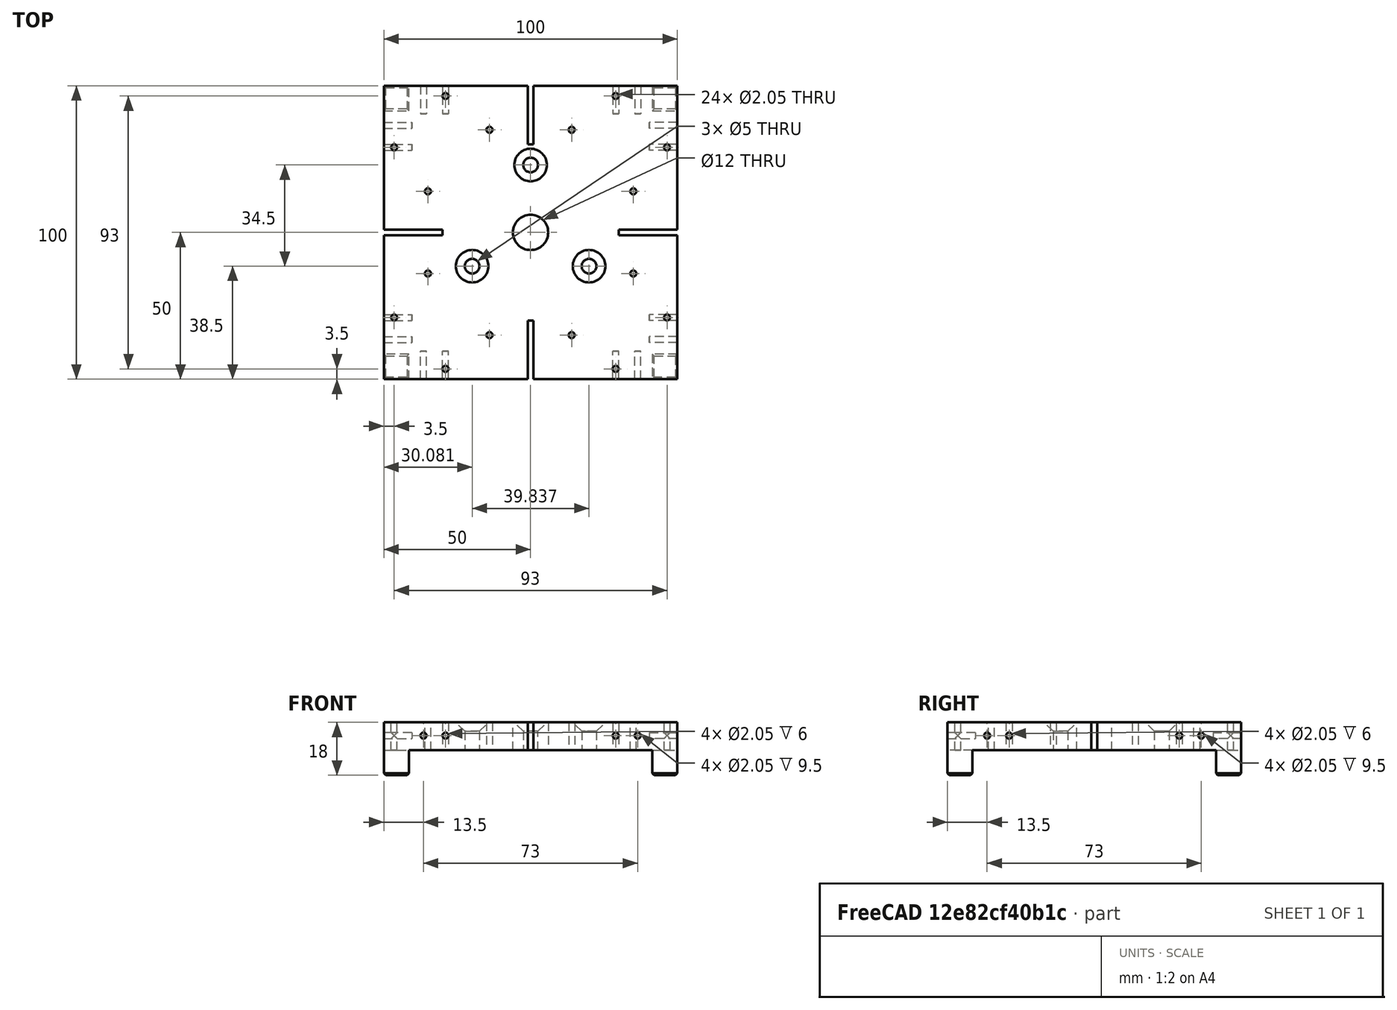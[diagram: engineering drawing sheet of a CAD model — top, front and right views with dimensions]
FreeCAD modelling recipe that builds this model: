
FCSTD DOCUMENT  (FreeCAD 0.20R29603 (Git))
Label: OpenSCAD_MyChassisModeling_NewBottom_version-cnes
License: All rights reserved
LicenseURL: http://en.wikipedia.org/wiki/All_rights_reserved
objects: Part::Fuse×65, Part::Box×61, Part::Cylinder×55, Part::MultiFuse×18, TechDraw::DrawViewDimension×18, Part::Cut×10, TechDraw::DrawViewPart×5, Part::Mirroring×4, TechDraw::DrawViewAnnotation×4, Part::Cone×3, TechDraw::DrawViewSection×2, Part::FeaturePython×1, TechDraw::DrawSVGTemplate×1, TechDraw::DrawPage×1
note: 217 computed .brp shape members not serialized (recipe doc carries the construction recipe); baked Part::Feature solids carry a one-line shape summary decoded from their .brp

FEATURE [Part::Box] cube
  AttacherType = Attacher::AttachEngine3D
  Height = 18
  Length = 8.5
  Placement = pos=(-4.25,-4.25,-18) rot=(0,0,1;0rad)
  Width = 8.5
FEATURE [Part::Box] cube001
  AttacherType = Attacher::AttachEngine3D
  Height = 100
  Length = 9.5
  Placement = pos=(-4.75,42.3466,-38.7141) rot=(1,0,0;0.785398rad)
  Width = 9.5
FEATURE [Part::Box] cube002
  AttacherType = Attacher::AttachEngine3D
  Height = 100
  Length = 9.5
  Placement = pos=(-42.3466,-4.75,-38.7141) rot=(0.357407,0.357407,0.862856;1.71777rad)
  Width = 9.5
FEATURE [Part::Fuse] Group
  Base = -> cube001
  Tool = -> cube002
FEATURE [Part::Box] cube003
  AttacherType = Attacher::AttachEngine3D
  Height = 100
  Length = 9.5
  Placement = pos=(-4.75,42.3466,-38.7141) rot=(1,0,0;0.785398rad)
  Width = 9.5
FEATURE [Part::Box] cube004
  AttacherType = Attacher::AttachEngine3D
  Height = 100
  Length = 9.5
  Placement = pos=(4.75,-42.3466,-38.7141) rot=(0,0.382683,0.92388;3.14159rad)
  Width = 9.5
FEATURE [Part::Fuse] Group001
  Base = -> cube003
  Tool = -> cube004
FEATURE [Part::Box] cube005
  AttacherType = Attacher::AttachEngine3D
  Height = 100
  Length = 9.5
  Placement = pos=(-4.75,42.3466,-38.7141) rot=(1,0,0;0.785398rad)
  Width = 9.5
FEATURE [Part::Box] cube006
  AttacherType = Attacher::AttachEngine3D
  Height = 100
  Length = 9.5
  Placement = pos=(42.3466,4.75,-38.7141) rot=(0.357407,-0.357407,-0.862856;1.71777rad)
  Width = 9.5
FEATURE [Part::Fuse] Group002
  Base = -> cube005
  Tool = -> cube006
FEATURE [Part::MultiFuse] Group003
  Shapes = -> [Group,Group001,Group002]
FEATURE [Part::Cut] difference
  Base = -> cube
  Placement = pos=(-45.75,-45.75,8.5) rot=(0,0,1;0rad)
  Tool = -> Group003
FEATURE [Part::Box] cube007
  AttacherType = Attacher::AttachEngine3D
  Height = 18
  Length = 8.5
  Placement = pos=(-4.25,-4.25,-18) rot=(0,0,1;0rad)
  Width = 8.5
FEATURE [Part::Box] cube008
  AttacherType = Attacher::AttachEngine3D
  Height = 100
  Length = 9.5
  Placement = pos=(-4.75,42.3466,-38.7141) rot=(1,0,0;0.785398rad)
  Width = 9.5
FEATURE [Part::Box] cube009
  AttacherType = Attacher::AttachEngine3D
  Height = 100
  Length = 9.5
  Placement = pos=(-42.3466,-4.75,-38.7141) rot=(0.357407,0.357407,0.862856;1.71777rad)
  Width = 9.5
FEATURE [Part::Fuse] Group004
  Base = -> cube008
  Tool = -> cube009
FEATURE [Part::Box] cube010
  AttacherType = Attacher::AttachEngine3D
  Height = 100
  Length = 9.5
  Placement = pos=(-4.75,42.3466,-38.7141) rot=(1,0,0;0.785398rad)
  Width = 9.5
FEATURE [Part::Box] cube011
  AttacherType = Attacher::AttachEngine3D
  Height = 100
  Length = 9.5
  Placement = pos=(4.75,-42.3466,-38.7141) rot=(0,0.382683,0.92388;3.14159rad)
  Width = 9.5
FEATURE [Part::Fuse] Group005
  Base = -> cube010
  Tool = -> cube011
FEATURE [Part::Box] cube012
  AttacherType = Attacher::AttachEngine3D
  Height = 100
  Length = 9.5
  Placement = pos=(-4.75,42.3466,-38.7141) rot=(1,0,0;0.785398rad)
  Width = 9.5
FEATURE [Part::Box] cube013
  AttacherType = Attacher::AttachEngine3D
  Height = 100
  Length = 9.5
  Placement = pos=(42.3466,4.75,-38.7141) rot=(0.357407,-0.357407,-0.862856;1.71777rad)
  Width = 9.5
FEATURE [Part::Fuse] Group006
  Base = -> cube012
  Tool = -> cube013
FEATURE [Part::MultiFuse] Group007
  Shapes = -> [Group004,Group005,Group006]
FEATURE [Part::Cut] difference001
  Base = -> cube007
  Placement = pos=(-45.75,-45.75,8.5) rot=(0,0,1;0rad)
  Tool = -> Group007
FEATURE [Part::Fuse] Group008
  Base = -> difference
  Tool = -> difference001
FEATURE [Part::Box] cube014
  AttacherType = Attacher::AttachEngine3D
  Height = 18
  Length = 8.5
  Placement = pos=(-4.25,-4.25,-18) rot=(0,0,1;0rad)
  Width = 8.5
FEATURE [Part::Box] cube015
  AttacherType = Attacher::AttachEngine3D
  Height = 100
  Length = 9.5
  Placement = pos=(-4.75,42.3466,-38.7141) rot=(1,0,0;0.785398rad)
  Width = 9.5
FEATURE [Part::Box] cube016
  AttacherType = Attacher::AttachEngine3D
  Height = 100
  Length = 9.5
  Placement = pos=(-42.3466,-4.75,-38.7141) rot=(0.357407,0.357407,0.862856;1.71777rad)
  Width = 9.5
FEATURE [Part::Fuse] Group009
  Base = -> cube015
  Tool = -> cube016
FEATURE [Part::Box] cube017
  AttacherType = Attacher::AttachEngine3D
  Height = 100
  Length = 9.5
  Placement = pos=(-4.75,42.3466,-38.7141) rot=(1,0,0;0.785398rad)
  Width = 9.5
FEATURE [Part::Box] cube018
  AttacherType = Attacher::AttachEngine3D
  Height = 100
  Length = 9.5
  Placement = pos=(4.75,-42.3466,-38.7141) rot=(0,0.382683,0.92388;3.14159rad)
  Width = 9.5
FEATURE [Part::Fuse] Group010
  Base = -> cube017
  Tool = -> cube018
FEATURE [Part::Box] cube019
  AttacherType = Attacher::AttachEngine3D
  Height = 100
  Length = 9.5
  Placement = pos=(-4.75,42.3466,-38.7141) rot=(1,0,0;0.785398rad)
  Width = 9.5
FEATURE [Part::Box] cube020
  AttacherType = Attacher::AttachEngine3D
  Height = 100
  Length = 9.5
  Placement = pos=(42.3466,4.75,-38.7141) rot=(0.357407,-0.357407,-0.862856;1.71777rad)
  Width = 9.5
FEATURE [Part::Fuse] Group011
  Base = -> cube019
  Tool = -> cube020
FEATURE [Part::MultiFuse] Group012
  Shapes = -> [Group009,Group010,Group011]
FEATURE [Part::Cut] difference002
  Base = -> cube014
  Placement = pos=(-45.75,-45.75,8.5) rot=(0,0,1;0rad)
  Tool = -> Group012
FEATURE [Part::Box] cube021
  AttacherType = Attacher::AttachEngine3D
  Height = 18
  Length = 8.5
  Placement = pos=(-4.25,-4.25,-18) rot=(0,0,1;0rad)
  Width = 8.5
FEATURE [Part::Box] cube022
  AttacherType = Attacher::AttachEngine3D
  Height = 100
  Length = 9.5
  Placement = pos=(-4.75,42.3466,-38.7141) rot=(1,0,0;0.785398rad)
  Width = 9.5
FEATURE [Part::Box] cube023
  AttacherType = Attacher::AttachEngine3D
  Height = 100
  Length = 9.5
  Placement = pos=(-42.3466,-4.75,-38.7141) rot=(0.357407,0.357407,0.862856;1.71777rad)
  Width = 9.5
FEATURE [Part::Fuse] Group013
  Base = -> cube022
  Tool = -> cube023
FEATURE [Part::Box] cube024
  AttacherType = Attacher::AttachEngine3D
  Height = 100
  Length = 9.5
  Placement = pos=(-4.75,42.3466,-38.7141) rot=(1,0,0;0.785398rad)
  Width = 9.5
FEATURE [Part::Box] cube025
  AttacherType = Attacher::AttachEngine3D
  Height = 100
  Length = 9.5
  Placement = pos=(4.75,-42.3466,-38.7141) rot=(0,0.382683,0.92388;3.14159rad)
  Width = 9.5
FEATURE [Part::Fuse] Group014
  Base = -> cube024
  Tool = -> cube025
FEATURE [Part::Box] cube026
  AttacherType = Attacher::AttachEngine3D
  Height = 100
  Length = 9.5
  Placement = pos=(-4.75,42.3466,-38.7141) rot=(1,0,0;0.785398rad)
  Width = 9.5
FEATURE [Part::Box] cube027
  AttacherType = Attacher::AttachEngine3D
  Height = 100
  Length = 9.5
  Placement = pos=(42.3466,4.75,-38.7141) rot=(0.357407,-0.357407,-0.862856;1.71777rad)
  Width = 9.5
FEATURE [Part::Fuse] Group015
  Base = -> cube026
  Tool = -> cube027
FEATURE [Part::MultiFuse] Group016
  Shapes = -> [Group013,Group014,Group015]
FEATURE [Part::Cut] difference003
  Base = -> cube021
  Placement = pos=(45.75,-45.75,8.5) rot=(0,0,1;1.5708rad)
  Tool = -> Group016
FEATURE [Part::Fuse] Group017
  Base = -> difference002
  Tool = -> difference003
FEATURE [Part::Box] cube028
  AttacherType = Attacher::AttachEngine3D
  Height = 18
  Length = 8.5
  Placement = pos=(-4.25,-4.25,-18) rot=(0,0,1;0rad)
  Width = 8.5
FEATURE [Part::Box] cube029
  AttacherType = Attacher::AttachEngine3D
  Height = 100
  Length = 9.5
  Placement = pos=(-4.75,42.3466,-38.7141) rot=(1,0,0;0.785398rad)
  Width = 9.5
FEATURE [Part::Box] cube030
  AttacherType = Attacher::AttachEngine3D
  Height = 100
  Length = 9.5
  Placement = pos=(-42.3466,-4.75,-38.7141) rot=(0.357407,0.357407,0.862856;1.71777rad)
  Width = 9.5
FEATURE [Part::Fuse] Group018
  Base = -> cube029
  Tool = -> cube030
FEATURE [Part::Box] cube031
  AttacherType = Attacher::AttachEngine3D
  Height = 100
  Length = 9.5
  Placement = pos=(-4.75,42.3466,-38.7141) rot=(1,0,0;0.785398rad)
  Width = 9.5
FEATURE [Part::Box] cube032
  AttacherType = Attacher::AttachEngine3D
  Height = 100
  Length = 9.5
  Placement = pos=(4.75,-42.3466,-38.7141) rot=(0,0.382683,0.92388;3.14159rad)
  Width = 9.5
FEATURE [Part::Fuse] Group019
  Base = -> cube031
  Tool = -> cube032
FEATURE [Part::Box] cube033
  AttacherType = Attacher::AttachEngine3D
  Height = 100
  Length = 9.5
  Placement = pos=(-4.75,42.3466,-38.7141) rot=(1,0,0;0.785398rad)
  Width = 9.5
FEATURE [Part::Box] cube034
  AttacherType = Attacher::AttachEngine3D
  Height = 100
  Length = 9.5
  Placement = pos=(42.3466,4.75,-38.7141) rot=(0.357407,-0.357407,-0.862856;1.71777rad)
  Width = 9.5
FEATURE [Part::Fuse] Group020
  Base = -> cube033
  Tool = -> cube034
FEATURE [Part::MultiFuse] Group021
  Shapes = -> [Group018,Group019,Group020]
FEATURE [Part::Cut] difference004
  Base = -> cube028
  Placement = pos=(-45.75,-45.75,8.5) rot=(0,0,1;0rad)
  Tool = -> Group021
FEATURE [Part::Box] cube035
  AttacherType = Attacher::AttachEngine3D
  Height = 18
  Length = 8.5
  Placement = pos=(-4.25,-4.25,-18) rot=(0,0,1;0rad)
  Width = 8.5
FEATURE [Part::Box] cube036
  AttacherType = Attacher::AttachEngine3D
  Height = 100
  Length = 9.5
  Placement = pos=(-4.75,42.3466,-38.7141) rot=(1,0,0;0.785398rad)
  Width = 9.5
FEATURE [Part::Box] cube037
  AttacherType = Attacher::AttachEngine3D
  Height = 100
  Length = 9.5
  Placement = pos=(-42.3466,-4.75,-38.7141) rot=(0.357407,0.357407,0.862856;1.71777rad)
  Width = 9.5
FEATURE [Part::Fuse] Group022
  Base = -> cube036
  Tool = -> cube037
FEATURE [Part::Box] cube038
  AttacherType = Attacher::AttachEngine3D
  Height = 100
  Length = 9.5
  Placement = pos=(-4.75,42.3466,-38.7141) rot=(1,0,0;0.785398rad)
  Width = 9.5
FEATURE [Part::Box] cube039
  AttacherType = Attacher::AttachEngine3D
  Height = 100
  Length = 9.5
  Placement = pos=(4.75,-42.3466,-38.7141) rot=(0,0.382683,0.92388;3.14159rad)
  Width = 9.5
FEATURE [Part::Fuse] Group023
  Base = -> cube038
  Tool = -> cube039
FEATURE [Part::Box] cube040
  AttacherType = Attacher::AttachEngine3D
  Height = 100
  Length = 9.5
  Placement = pos=(-4.75,42.3466,-38.7141) rot=(1,0,0;0.785398rad)
  Width = 9.5
FEATURE [Part::Box] cube041
  AttacherType = Attacher::AttachEngine3D
  Height = 100
  Length = 9.5
  Placement = pos=(42.3466,4.75,-38.7141) rot=(0.357407,-0.357407,-0.862856;1.71777rad)
  Width = 9.5
FEATURE [Part::Fuse] Group024
  Base = -> cube040
  Tool = -> cube041
FEATURE [Part::MultiFuse] Group025
  Shapes = -> [Group022,Group023,Group024]
FEATURE [Part::Cut] difference005
  Base = -> cube035
  Placement = pos=(45.75,45.75,8.5) rot=(0,0,1;3.14159rad)
  Tool = -> Group025
FEATURE [Part::Fuse] Group026
  Base = -> difference004
  Tool = -> difference005
FEATURE [Part::Box] cube042
  AttacherType = Attacher::AttachEngine3D
  Height = 18
  Length = 8.5
  Placement = pos=(-4.25,-4.25,-18) rot=(0,0,1;0rad)
  Width = 8.5
FEATURE [Part::Box] cube043
  AttacherType = Attacher::AttachEngine3D
  Height = 100
  Length = 9.5
  Placement = pos=(-4.75,42.3466,-38.7141) rot=(1,0,0;0.785398rad)
  Width = 9.5
FEATURE [Part::Box] cube044
  AttacherType = Attacher::AttachEngine3D
  Height = 100
  Length = 9.5
  Placement = pos=(-42.3466,-4.75,-38.7141) rot=(0.357407,0.357407,0.862856;1.71777rad)
  Width = 9.5
FEATURE [Part::Fuse] Group027
  Base = -> cube043
  Tool = -> cube044
FEATURE [Part::Box] cube045
  AttacherType = Attacher::AttachEngine3D
  Height = 100
  Length = 9.5
  Placement = pos=(-4.75,42.3466,-38.7141) rot=(1,0,0;0.785398rad)
  Width = 9.5
FEATURE [Part::Box] cube046
  AttacherType = Attacher::AttachEngine3D
  Height = 100
  Length = 9.5
  Placement = pos=(4.75,-42.3466,-38.7141) rot=(0,0.382683,0.92388;3.14159rad)
  Width = 9.5
FEATURE [Part::Fuse] Group028
  Base = -> cube045
  Tool = -> cube046
FEATURE [Part::Box] cube047
  AttacherType = Attacher::AttachEngine3D
  Height = 100
  Length = 9.5
  Placement = pos=(-4.75,42.3466,-38.7141) rot=(1,0,0;0.785398rad)
  Width = 9.5
FEATURE [Part::Box] cube048
  AttacherType = Attacher::AttachEngine3D
  Height = 100
  Length = 9.5
  Placement = pos=(42.3466,4.75,-38.7141) rot=(0.357407,-0.357407,-0.862856;1.71777rad)
  Width = 9.5
FEATURE [Part::Fuse] Group029
  Base = -> cube047
  Tool = -> cube048
FEATURE [Part::MultiFuse] Group030
  Shapes = -> [Group027,Group028,Group029]
FEATURE [Part::Cut] difference006
  Base = -> cube042
  Placement = pos=(-45.75,-45.75,8.5) rot=(0,0,1;0rad)
  Tool = -> Group030
FEATURE [Part::Box] cube049
  AttacherType = Attacher::AttachEngine3D
  Height = 18
  Length = 8.5
  Placement = pos=(-4.25,-4.25,-18) rot=(0,0,1;0rad)
  Width = 8.5
FEATURE [Part::Box] cube050
  AttacherType = Attacher::AttachEngine3D
  Height = 100
  Length = 9.5
  Placement = pos=(-4.75,42.3466,-38.7141) rot=(1,0,0;0.785398rad)
  Width = 9.5
FEATURE [Part::Box] cube051
  AttacherType = Attacher::AttachEngine3D
  Height = 100
  Length = 9.5
  Placement = pos=(-42.3466,-4.75,-38.7141) rot=(0.357407,0.357407,0.862856;1.71777rad)
  Width = 9.5
FEATURE [Part::Fuse] Group031
  Base = -> cube050
  Tool = -> cube051
FEATURE [Part::Box] cube052
  AttacherType = Attacher::AttachEngine3D
  Height = 100
  Length = 9.5
  Placement = pos=(-4.75,42.3466,-38.7141) rot=(1,0,0;0.785398rad)
  Width = 9.5
FEATURE [Part::Box] cube053
  AttacherType = Attacher::AttachEngine3D
  Height = 100
  Length = 9.5
  Placement = pos=(4.75,-42.3466,-38.7141) rot=(0,0.382683,0.92388;3.14159rad)
  Width = 9.5
FEATURE [Part::Fuse] Group032
  Base = -> cube052
  Tool = -> cube053
FEATURE [Part::Box] cube054
  AttacherType = Attacher::AttachEngine3D
  Height = 100
  Length = 9.5
  Placement = pos=(-4.75,42.3466,-38.7141) rot=(1,0,0;0.785398rad)
  Width = 9.5
FEATURE [Part::Box] cube055
  AttacherType = Attacher::AttachEngine3D
  Height = 100
  Length = 9.5
  Placement = pos=(42.3466,4.75,-38.7141) rot=(0.357407,-0.357407,-0.862856;1.71777rad)
  Width = 9.5
FEATURE [Part::Fuse] Group033
  Base = -> cube054
  Tool = -> cube055
FEATURE [Part::MultiFuse] Group034
  Shapes = -> [Group031,Group032,Group033]
FEATURE [Part::Cut] difference007
  Base = -> cube049
  Placement = pos=(-45.75,45.75,8.5) rot=(0,0,-1;1.5708rad)
  Tool = -> Group034
FEATURE [Part::Fuse] Group035
  Base = -> difference006
  Tool = -> difference007
FEATURE [Part::MultiFuse] Group036
  Shapes = -> [Group008,Group017,Group026,Group035]
FEATURE [Part::Box] cube056
  AttacherType = Attacher::AttachEngine3D
  Height = 9.5
  Length = 100
  Placement = pos=(-50,-50,-9.5) rot=(0,0,1;0rad)
  Width = 100
FEATURE [Part::Cylinder] cylinder
  Angle = 360
  AttacherType = Attacher::AttachEngine3D
  FirstAngle = 0
  Height = 11
  Placement = pos=(40.5,-36.5,-5) rot=(0,1,0;1.5708rad)
  Radius = 1.025
  SecondAngle = 0
FEATURE [Part::Cylinder] cylinder001
  Angle = 360
  AttacherType = Attacher::AttachEngine3D
  FirstAngle = 0
  Height = 11
  Placement = pos=(40.5,-29,-5) rot=(0,1,0;1.5708rad)
  Radius = 1.025
  SecondAngle = 0
FEATURE [Part::Fuse] Group037
  Base = -> cylinder
  Tool = -> cylinder001
FEATURE [Part::Cylinder] cylinder002
  Angle = 360
  AttacherType = Attacher::AttachEngine3D
  FirstAngle = 0
  Height = 11
  Placement = pos=(40.5,-36.5,-5) rot=(0,1,0;1.5708rad)
  Radius = 1.025
  SecondAngle = 0
FEATURE [Part::Cylinder] cylinder003
  Angle = 360
  AttacherType = Attacher::AttachEngine3D
  FirstAngle = 0
  Height = 11
  Placement = pos=(40.5,-29,-5) rot=(0,1,0;1.5708rad)
  Radius = 1.025
  SecondAngle = 0
FEATURE [Part::Fuse] Group038
  Base = -> cylinder002
  Tool = -> cylinder003
FEATURE [Part::Mirroring] mirr_Group038  label="mirrored Group038"
  Base = (0,0,0)
  Normal = (0,1,0)
  Source = -> Group038
FEATURE [Part::Fuse] Group039
  Base = -> Group037
  Tool = -> mirr_Group038
FEATURE [Part::Cylinder] cylinder004
  Angle = 360
  AttacherType = Attacher::AttachEngine3D
  FirstAngle = 0
  Height = 11
  Placement = pos=(40.5,-36.5,-5) rot=(0,1,0;1.5708rad)
  Radius = 1.025
  SecondAngle = 0
FEATURE [Part::Cylinder] cylinder005
  Angle = 360
  AttacherType = Attacher::AttachEngine3D
  FirstAngle = 0
  Height = 11
  Placement = pos=(40.5,-29,-5) rot=(0,1,0;1.5708rad)
  Radius = 1.025
  SecondAngle = 0
FEATURE [Part::Fuse] Group040
  Base = -> cylinder004
  Tool = -> cylinder005
FEATURE [Part::Cylinder] cylinder006
  Angle = 360
  AttacherType = Attacher::AttachEngine3D
  FirstAngle = 0
  Height = 11
  Placement = pos=(40.5,-36.5,-5) rot=(0,1,0;1.5708rad)
  Radius = 1.025
  SecondAngle = 0
FEATURE [Part::Cylinder] cylinder007
  Angle = 360
  AttacherType = Attacher::AttachEngine3D
  FirstAngle = 0
  Height = 11
  Placement = pos=(40.5,-29,-5) rot=(0,1,0;1.5708rad)
  Radius = 1.025
  SecondAngle = 0
FEATURE [Part::Fuse] Group041
  Base = -> cylinder006
  Tool = -> cylinder007
FEATURE [Part::Mirroring] mirr_Group041  label="mirrored Group041"
  Base = (0,0,0)
  Normal = (0,1,0)
  Source = -> Group041
FEATURE [Part::Fuse] Group042
  Base = -> Group040
  Placement = pos=(0,0,0) rot=(0,0,1;1.5708rad)
  Tool = -> mirr_Group041
FEATURE [Part::Cylinder] cylinder008
  Angle = 360
  AttacherType = Attacher::AttachEngine3D
  FirstAngle = 0
  Height = 11
  Placement = pos=(40.5,-36.5,-5) rot=(0,1,0;1.5708rad)
  Radius = 1.025
  SecondAngle = 0
FEATURE [Part::Cylinder] cylinder009
  Angle = 360
  AttacherType = Attacher::AttachEngine3D
  FirstAngle = 0
  Height = 11
  Placement = pos=(40.5,-29,-5) rot=(0,1,0;1.5708rad)
  Radius = 1.025
  SecondAngle = 0
FEATURE [Part::Fuse] Group043
  Base = -> cylinder008
  Tool = -> cylinder009
FEATURE [Part::Cylinder] cylinder010
  Angle = 360
  AttacherType = Attacher::AttachEngine3D
  FirstAngle = 0
  Height = 11
  Placement = pos=(40.5,-36.5,-5) rot=(0,1,0;1.5708rad)
  Radius = 1.025
  SecondAngle = 0
FEATURE [Part::Cylinder] cylinder011
  Angle = 360
  AttacherType = Attacher::AttachEngine3D
  FirstAngle = 0
  Height = 11
  Placement = pos=(40.5,-29,-5) rot=(0,1,0;1.5708rad)
  Radius = 1.025
  SecondAngle = 0
FEATURE [Part::Fuse] Group044
  Base = -> cylinder010
  Tool = -> cylinder011
FEATURE [Part::Mirroring] mirr_Group044  label="mirrored Group044"
  Base = (0,0,0)
  Normal = (0,1,0)
  Source = -> Group044
FEATURE [Part::Fuse] Group045
  Base = -> Group043
  Placement = pos=(0,0,0) rot=(0,0,1;3.14159rad)
  Tool = -> mirr_Group044
FEATURE [Part::Cylinder] cylinder012
  Angle = 360
  AttacherType = Attacher::AttachEngine3D
  FirstAngle = 0
  Height = 11
  Placement = pos=(40.5,-36.5,-5) rot=(0,1,0;1.5708rad)
  Radius = 1.025
  SecondAngle = 0
FEATURE [Part::Cylinder] cylinder013
  Angle = 360
  AttacherType = Attacher::AttachEngine3D
  FirstAngle = 0
  Height = 11
  Placement = pos=(40.5,-29,-5) rot=(0,1,0;1.5708rad)
  Radius = 1.025
  SecondAngle = 0
FEATURE [Part::Fuse] Group046
  Base = -> cylinder012
  Tool = -> cylinder013
FEATURE [Part::Cylinder] cylinder014
  Angle = 360
  AttacherType = Attacher::AttachEngine3D
  FirstAngle = 0
  Height = 11
  Placement = pos=(40.5,-36.5,-5) rot=(0,1,0;1.5708rad)
  Radius = 1.025
  SecondAngle = 0
FEATURE [Part::Cylinder] cylinder015
  Angle = 360
  AttacherType = Attacher::AttachEngine3D
  FirstAngle = 0
  Height = 11
  Placement = pos=(40.5,-29,-5) rot=(0,1,0;1.5708rad)
  Radius = 1.025
  SecondAngle = 0
FEATURE [Part::Fuse] Group047
  Base = -> cylinder014
  Tool = -> cylinder015
FEATURE [Part::Mirroring] mirr_Group047  label="mirrored Group047"
  Base = (0,0,0)
  Normal = (0,1,0)
  Source = -> Group047
FEATURE [Part::Fuse] Group048
  Base = -> Group046
  Placement = pos=(0,0,0) rot=(0,0,-1;1.5708rad)
  Tool = -> mirr_Group047
FEATURE [Part::MultiFuse] Group049
  Shapes = -> [Group039,Group042,Group045,Group048]
FEATURE [Part::Cylinder] cylinder016
  Angle = 360
  AttacherType = Attacher::AttachEngine3D
  FirstAngle = 0
  Height = 100
  Placement = pos=(-29,0,-50) rot=(0,0,1;0rad)
  Radius = 1.025
  SecondAngle = 0
FEATURE [Part::Cylinder] cylinder017
  Angle = 360
  AttacherType = Attacher::AttachEngine3D
  FirstAngle = 0
  Height = 100
  Placement = pos=(29,0,-50) rot=(0,0,1;0rad)
  Radius = 1.025
  SecondAngle = 0
FEATURE [Part::Fuse] Matrix_Union
  Base = -> cylinder016
  Placement = pos=(0,46.5,0) rot=(0,0,1;0rad)
  Tool = -> cylinder017
FEATURE [Part::Cylinder] cylinder018
  Angle = 360
  AttacherType = Attacher::AttachEngine3D
  FirstAngle = 0
  Height = 100
  Placement = pos=(-29,0,-50) rot=(0,0,1;0rad)
  Radius = 1.025
  SecondAngle = 0
FEATURE [Part::Cylinder] cylinder019
  Angle = 360
  AttacherType = Attacher::AttachEngine3D
  FirstAngle = 0
  Height = 100
  Placement = pos=(29,0,-50) rot=(0,0,1;0rad)
  Radius = 1.025
  SecondAngle = 0
FEATURE [Part::Fuse] Matrix_Union001
  Base = -> cylinder018
  Placement = pos=(0,46.5,0) rot=(0,0,1;0rad)
  Tool = -> cylinder019
FEATURE [Part::Fuse] Group050
  Base = -> Matrix_Union
  Tool = -> Matrix_Union001
FEATURE [Part::Cylinder] cylinder020
  Angle = 360
  AttacherType = Attacher::AttachEngine3D
  FirstAngle = 0
  Height = 100
  Placement = pos=(-29,0,-50) rot=(0,0,1;0rad)
  Radius = 1.025
  SecondAngle = 0
FEATURE [Part::Cylinder] cylinder021
  Angle = 360
  AttacherType = Attacher::AttachEngine3D
  FirstAngle = 0
  Height = 100
  Placement = pos=(29,0,-50) rot=(0,0,1;0rad)
  Radius = 1.025
  SecondAngle = 0
FEATURE [Part::Fuse] Matrix_Union002
  Base = -> cylinder020
  Placement = pos=(0,46.5,0) rot=(0,0,1;0rad)
  Tool = -> cylinder021
FEATURE [Part::Cylinder] cylinder022
  Angle = 360
  AttacherType = Attacher::AttachEngine3D
  FirstAngle = 0
  Height = 100
  Placement = pos=(-29,0,-50) rot=(0,0,1;0rad)
  Radius = 1.025
  SecondAngle = 0
FEATURE [Part::Cylinder] cylinder023
  Angle = 360
  AttacherType = Attacher::AttachEngine3D
  FirstAngle = 0
  Height = 100
  Placement = pos=(29,0,-50) rot=(0,0,1;0rad)
  Radius = 1.025
  SecondAngle = 0
FEATURE [Part::Fuse] Matrix_Union003
  Base = -> cylinder022
  Placement = pos=(-46.5,0,0) rot=(0,0,1;1.5708rad)
  Tool = -> cylinder023
FEATURE [Part::Fuse] Group051
  Base = -> Matrix_Union002
  Tool = -> Matrix_Union003
FEATURE [Part::Cylinder] cylinder024
  Angle = 360
  AttacherType = Attacher::AttachEngine3D
  FirstAngle = 0
  Height = 100
  Placement = pos=(-29,0,-50) rot=(0,0,1;0rad)
  Radius = 1.025
  SecondAngle = 0
FEATURE [Part::Cylinder] cylinder025
  Angle = 360
  AttacherType = Attacher::AttachEngine3D
  FirstAngle = 0
  Height = 100
  Placement = pos=(29,0,-50) rot=(0,0,1;0rad)
  Radius = 1.025
  SecondAngle = 0
FEATURE [Part::Fuse] Matrix_Union004
  Base = -> cylinder024
  Placement = pos=(0,46.5,0) rot=(0,0,1;0rad)
  Tool = -> cylinder025
FEATURE [Part::Cylinder] cylinder026
  Angle = 360
  AttacherType = Attacher::AttachEngine3D
  FirstAngle = 0
  Height = 100
  Placement = pos=(-29,0,-50) rot=(0,0,1;0rad)
  Radius = 1.025
  SecondAngle = 0
FEATURE [Part::Cylinder] cylinder027
  Angle = 360
  AttacherType = Attacher::AttachEngine3D
  FirstAngle = 0
  Height = 100
  Placement = pos=(29,0,-50) rot=(0,0,1;0rad)
  Radius = 1.025
  SecondAngle = 0
FEATURE [Part::Fuse] Matrix_Union005
  Base = -> cylinder026
  Placement = pos=(-6e-15,-46.5,0) rot=(0,0,1;3.14159rad)
  Tool = -> cylinder027
FEATURE [Part::Fuse] Group052
  Base = -> Matrix_Union004
  Tool = -> Matrix_Union005
FEATURE [Part::Cylinder] cylinder028
  Angle = 360
  AttacherType = Attacher::AttachEngine3D
  FirstAngle = 0
  Height = 100
  Placement = pos=(-29,0,-50) rot=(0,0,1;0rad)
  Radius = 1.025
  SecondAngle = 0
FEATURE [Part::Cylinder] cylinder029
  Angle = 360
  AttacherType = Attacher::AttachEngine3D
  FirstAngle = 0
  Height = 100
  Placement = pos=(29,0,-50) rot=(0,0,1;0rad)
  Radius = 1.025
  SecondAngle = 0
FEATURE [Part::Fuse] Matrix_Union006
  Base = -> cylinder028
  Placement = pos=(0,46.5,0) rot=(0,0,1;0rad)
  Tool = -> cylinder029
FEATURE [Part::Cylinder] cylinder030
  Angle = 360
  AttacherType = Attacher::AttachEngine3D
  FirstAngle = 0
  Height = 100
  Placement = pos=(-29,0,-50) rot=(0,0,1;0rad)
  Radius = 1.025
  SecondAngle = 0
FEATURE [Part::Cylinder] cylinder031
  Angle = 360
  AttacherType = Attacher::AttachEngine3D
  FirstAngle = 0
  Height = 100
  Placement = pos=(29,0,-50) rot=(0,0,1;0rad)
  Radius = 1.025
  SecondAngle = 0
FEATURE [Part::Fuse] Matrix_Union007
  Base = -> cylinder030
  Placement = pos=(46.5,0,0) rot=(0,0,-1;1.5708rad)
  Tool = -> cylinder031
FEATURE [Part::Fuse] Group053
  Base = -> Matrix_Union006
  Tool = -> Matrix_Union007
FEATURE [Part::MultiFuse] Group054
  Shapes = -> [Group050,Group051,Group052,Group053]
FEATURE [Part::Cylinder] cylinder032
  Angle = 360
  AttacherType = Attacher::AttachEngine3D
  FirstAngle = 0
  Height = 100
  Placement = pos=(-14,0,-50) rot=(0,0,1;0rad)
  Radius = 1.025
  SecondAngle = 0
FEATURE [Part::Cylinder] cylinder033
  Angle = 360
  AttacherType = Attacher::AttachEngine3D
  FirstAngle = 0
  Height = 100
  Placement = pos=(14,0,-50) rot=(0,0,1;0rad)
  Radius = 1.025
  SecondAngle = 0
FEATURE [Part::Fuse] Matrix_Union008
  Base = -> cylinder032
  Placement = pos=(0,35,0) rot=(0,0,1;0rad)
  Tool = -> cylinder033
FEATURE [Part::Cylinder] cylinder034
  Angle = 360
  AttacherType = Attacher::AttachEngine3D
  FirstAngle = 0
  Height = 100
  Placement = pos=(-14,0,-50) rot=(0,0,1;0rad)
  Radius = 1.025
  SecondAngle = 0
FEATURE [Part::Cylinder] cylinder035
  Angle = 360
  AttacherType = Attacher::AttachEngine3D
  FirstAngle = 0
  Height = 100
  Placement = pos=(14,0,-50) rot=(0,0,1;0rad)
  Radius = 1.025
  SecondAngle = 0
FEATURE [Part::Fuse] Matrix_Union009
  Base = -> cylinder034
  Placement = pos=(0,35,0) rot=(0,0,1;0rad)
  Tool = -> cylinder035
FEATURE [Part::Fuse] Group055
  Base = -> Matrix_Union008
  Tool = -> Matrix_Union009
FEATURE [Part::Cylinder] cylinder036
  Angle = 360
  AttacherType = Attacher::AttachEngine3D
  FirstAngle = 0
  Height = 100
  Placement = pos=(-14,0,-50) rot=(0,0,1;0rad)
  Radius = 1.025
  SecondAngle = 0
FEATURE [Part::Cylinder] cylinder037
  Angle = 360
  AttacherType = Attacher::AttachEngine3D
  FirstAngle = 0
  Height = 100
  Placement = pos=(14,0,-50) rot=(0,0,1;0rad)
  Radius = 1.025
  SecondAngle = 0
FEATURE [Part::Fuse] Matrix_Union010
  Base = -> cylinder036
  Placement = pos=(0,35,0) rot=(0,0,1;0rad)
  Tool = -> cylinder037
FEATURE [Part::Cylinder] cylinder038
  Angle = 360
  AttacherType = Attacher::AttachEngine3D
  FirstAngle = 0
  Height = 100
  Placement = pos=(-14,0,-50) rot=(0,0,1;0rad)
  Radius = 1.025
  SecondAngle = 0
FEATURE [Part::Cylinder] cylinder039
  Angle = 360
  AttacherType = Attacher::AttachEngine3D
  FirstAngle = 0
  Height = 100
  Placement = pos=(14,0,-50) rot=(0,0,1;0rad)
  Radius = 1.025
  SecondAngle = 0
FEATURE [Part::Fuse] Matrix_Union011
  Base = -> cylinder038
  Placement = pos=(-35,0,0) rot=(0,0,1;1.5708rad)
  Tool = -> cylinder039
FEATURE [Part::Fuse] Group056
  Base = -> Matrix_Union010
  Tool = -> Matrix_Union011
FEATURE [Part::Cylinder] cylinder040
  Angle = 360
  AttacherType = Attacher::AttachEngine3D
  FirstAngle = 0
  Height = 100
  Placement = pos=(-14,0,-50) rot=(0,0,1;0rad)
  Radius = 1.025
  SecondAngle = 0
FEATURE [Part::Cylinder] cylinder041
  Angle = 360
  AttacherType = Attacher::AttachEngine3D
  FirstAngle = 0
  Height = 100
  Placement = pos=(14,0,-50) rot=(0,0,1;0rad)
  Radius = 1.025
  SecondAngle = 0
FEATURE [Part::Fuse] Matrix_Union012
  Base = -> cylinder040
  Placement = pos=(0,35,0) rot=(0,0,1;0rad)
  Tool = -> cylinder041
FEATURE [Part::Cylinder] cylinder042
  Angle = 360
  AttacherType = Attacher::AttachEngine3D
  FirstAngle = 0
  Height = 100
  Placement = pos=(-14,0,-50) rot=(0,0,1;0rad)
  Radius = 1.025
  SecondAngle = 0
FEATURE [Part::Cylinder] cylinder043
  Angle = 360
  AttacherType = Attacher::AttachEngine3D
  FirstAngle = 0
  Height = 100
  Placement = pos=(14,0,-50) rot=(0,0,1;0rad)
  Radius = 1.025
  SecondAngle = 0
FEATURE [Part::Fuse] Matrix_Union013
  Base = -> cylinder042
  Placement = pos=(-4e-15,-35,0) rot=(0,0,1;3.14159rad)
  Tool = -> cylinder043
FEATURE [Part::Fuse] Group057
  Base = -> Matrix_Union012
  Tool = -> Matrix_Union013
FEATURE [Part::Cylinder] cylinder044
  Angle = 360
  AttacherType = Attacher::AttachEngine3D
  FirstAngle = 0
  Height = 100
  Placement = pos=(-14,0,-50) rot=(0,0,1;0rad)
  Radius = 1.025
  SecondAngle = 0
FEATURE [Part::Cylinder] cylinder045
  Angle = 360
  AttacherType = Attacher::AttachEngine3D
  FirstAngle = 0
  Height = 100
  Placement = pos=(14,0,-50) rot=(0,0,1;0rad)
  Radius = 1.025
  SecondAngle = 0
FEATURE [Part::Fuse] Matrix_Union014
  Base = -> cylinder044
  Placement = pos=(0,35,0) rot=(0,0,1;0rad)
  Tool = -> cylinder045
FEATURE [Part::Cylinder] cylinder046
  Angle = 360
  AttacherType = Attacher::AttachEngine3D
  FirstAngle = 0
  Height = 100
  Placement = pos=(-14,0,-50) rot=(0,0,1;0rad)
  Radius = 1.025
  SecondAngle = 0
FEATURE [Part::Cylinder] cylinder047
  Angle = 360
  AttacherType = Attacher::AttachEngine3D
  FirstAngle = 0
  Height = 100
  Placement = pos=(14,0,-50) rot=(0,0,1;0rad)
  Radius = 1.025
  SecondAngle = 0
FEATURE [Part::Fuse] Matrix_Union015
  Base = -> cylinder046
  Placement = pos=(35,0,0) rot=(0,0,-1;1.5708rad)
  Tool = -> cylinder047
FEATURE [Part::Fuse] Group058
  Base = -> Matrix_Union014
  Tool = -> Matrix_Union015
FEATURE [Part::MultiFuse] Group059
  Shapes = -> [Group055,Group056,Group057,Group058]
FEATURE [Part::MultiFuse] union
  Shapes = -> [Group049,Group054,Group059]
FEATURE [Part::Cut] difference008
  Base = -> cube056
  Tool = -> union
FEATURE [Part::Fuse] union001
  Base = -> Group036
  Tool = -> difference008
FEATURE [Part::Cone] cylinder048
  Angle = 360
  AttacherType = Attacher::AttachEngine3D
  Height = 5.55
  Placement = pos=(0,0,-5.55) rot=(0,0,1;0rad)
  Radius1 = 0
  Radius2 = 5.55
FEATURE [Part::Cylinder] cylinder049
  Angle = 360
  AttacherType = Attacher::AttachEngine3D
  FirstAngle = 0
  Height = 0.5
  Radius = 5.55
  SecondAngle = 0
FEATURE [Part::Cylinder] cylinder050
  Angle = 360
  AttacherType = Attacher::AttachEngine3D
  FirstAngle = 0
  Height = 45
  Placement = pos=(0,0,-45) rot=(0,0,1;0rad)
  Radius = 2.5
  SecondAngle = 0
FEATURE [Part::MultiFuse] union002
  Placement = pos=(0,-23,-9.5) rot=(1,0,0;3.14159rad)
  Shapes = -> [cylinder048,cylinder049,cylinder050]
FEATURE [Part::Cone] cylinder051
  Angle = 360
  AttacherType = Attacher::AttachEngine3D
  Height = 5.55
  Placement = pos=(0,0,-5.55) rot=(0,0,1;0rad)
  Radius1 = 0
  Radius2 = 5.55
FEATURE [Part::Cylinder] cylinder052
  Angle = 360
  AttacherType = Attacher::AttachEngine3D
  FirstAngle = 0
  Height = 0.5
  Radius = 5.55
  SecondAngle = 0
FEATURE [Part::Cylinder] cylinder053
  Angle = 360
  AttacherType = Attacher::AttachEngine3D
  FirstAngle = 0
  Height = 45
  Placement = pos=(0,0,-45) rot=(0,0,1;0rad)
  Radius = 2.5
  SecondAngle = 0
FEATURE [Part::MultiFuse] union003
  Placement = pos=(19.9186,11.5,-9.5) rot=(0.5,0.866025,0;3.14159rad)
  Shapes = -> [cylinder051,cylinder052,cylinder053]
FEATURE [Part::Cone] cylinder054
  Angle = 360
  AttacherType = Attacher::AttachEngine3D
  Height = 5.55
  Placement = pos=(0,0,-5.55) rot=(0,0,1;0rad)
  Radius1 = 0
  Radius2 = 5.55
FEATURE [Part::Cylinder] cylinder055
  Angle = 360
  AttacherType = Attacher::AttachEngine3D
  FirstAngle = 0
  Height = 0.5
  Radius = 5.55
  SecondAngle = 0
FEATURE [Part::Cylinder] cylinder056
  Angle = 360
  AttacherType = Attacher::AttachEngine3D
  FirstAngle = 0
  Height = 45
  Placement = pos=(0,0,-45) rot=(0,0,1;0rad)
  Radius = 2.5
  SecondAngle = 0
FEATURE [Part::MultiFuse] union004
  Placement = pos=(-19.9186,11.5,-9.5) rot=(-0.5,0.866025,0;3.14159rad)
  Shapes = -> [cylinder054,cylinder055,cylinder056]
FEATURE [Part::Box] cube057
  AttacherType = Attacher::AttachEngine3D
  Height = 100
  Length = 100
  Placement = pos=(30,-1,-50) rot=(0,0,1;0rad)
  Width = 2
FEATURE [Part::Box] cube058
  AttacherType = Attacher::AttachEngine3D
  Height = 100
  Length = 100
  Placement = pos=(1,30,-50) rot=(0,0,1;1.5708rad)
  Width = 2
FEATURE [Part::Box] cube059
  AttacherType = Attacher::AttachEngine3D
  Height = 100
  Length = 100
  Placement = pos=(-30,1,-50) rot=(0,0,1;3.14159rad)
  Width = 2
FEATURE [Part::Box] cube060
  AttacherType = Attacher::AttachEngine3D
  Height = 100
  Length = 100
  Placement = pos=(-1,-30,-50) rot=(0,0,-1;1.5708rad)
  Width = 2
FEATURE [Part::MultiFuse] union005
  Shapes = -> [cube057,cube058,cube059,cube060]
FEATURE [Part::Cylinder] cylinder057
  Angle = 360
  AttacherType = Attacher::AttachEngine3D
  FirstAngle = 0
  Height = 500
  Placement = pos=(0,0,-250) rot=(0,0,1;0rad)
  Radius = 6
  SecondAngle = 0
FEATURE [Part::MultiFuse] union006
  Shapes = -> [union002,union003,union004,union005,cylinder057]
FEATURE [Part::Cut] difference009
  Base = -> union001
  Tool = -> union006
FEATURE [Part::FeaturePython] refine  label="refine_difference009"  # WARN: FeaturePython — macro-defined, semantics opaque (R4)
  Base = -> difference009
  Placement = pos=(0,0,0) rot=(1,0,0;3.14159rad)
FEATURE [TechDraw::DrawSVGTemplate] Template
  Height = 297
  Orientation = 1
  Width = 420
FEATURE [TechDraw::DrawViewPart] View  label="Top View"
  CoarseView = false
  Direction = (0,0,1)
  Focus = 100
  HardHidden = false
  IsoCount = 0
  IsoHidden = false
  IsoVisible = false
  LockPosition = false
  Perspective = false
  Rotation = 0
  ScaleType = 0
  SeamHidden = false
  SeamVisible = true
  SmoothHidden = false
  SmoothVisible = true
  Source = -> [refine]
  X = 68.2825
  XDirection = (1,0,0)
  Y = 225
FEATURE [TechDraw::DrawViewPart] View001  label="Bottom View"
  CoarseView = false
  Direction = (0,0,-1)
  Focus = 100
  HardHidden = false
  IsoCount = 0
  IsoHidden = false
  IsoVisible = false
  LockPosition = false
  Perspective = false
  Rotation = 0
  ScaleType = 0
  SeamHidden = false
  SeamVisible = true
  SmoothHidden = false
  SmoothVisible = true
  Source = -> [refine]
  X = 198.378
  XDirection = (1,0,0)
  Y = 225
FEATURE [TechDraw::DrawViewPart] View003  label="Upper Right"
  CoarseView = false
  Direction = (0.707,-0.5,0.5)
  Focus = 100
  HardHidden = false
  IsoCount = 0
  IsoHidden = false
  IsoVisible = false
  LockPosition = false
  Perspective = false
  Rotation = 0
  ScaleType = 0
  SeamHidden = false
  SeamVisible = true
  SmoothHidden = false
  SmoothVisible = true
  Source = -> [refine]
  X = 337
  XDirection = (0.707,0.5,-0.5)
  Y = 225
FEATURE [TechDraw::DrawViewDimension] Dimension  label="Dimension_X"
  AngleOverride = false
  Arbitrary = false
  ArbitraryTolerances = false
  EqualTolerance = true
  ExtensionAngle = 0
  FormatSpec = %.2w
  FormatSpecOverTolerance = %+.2w
  FormatSpecUnderTolerance = %+.2w
  Inverted = false
  LineAngle = 0
  LockPosition = false
  MeasureType = 1
  OverTolerance = 0
  References2D = -> [View]
  Rotation = 0
  ScaleType = 0
  TheoreticalExact = false
  Type = 1
  UnderTolerance = 0
  X = 0
  Y = -65
FEATURE [TechDraw::DrawViewDimension] Dimension001  label="Dimension_Y"
  AngleOverride = false
  Arbitrary = false
  ArbitraryTolerances = false
  EqualTolerance = true
  ExtensionAngle = 0
  FormatSpec = %.2w
  FormatSpecOverTolerance = %+.2w
  FormatSpecUnderTolerance = %+.2w
  Inverted = false
  LineAngle = 0
  LockPosition = false
  MeasureType = 1
  OverTolerance = 0
  References2D = -> [View]
  Rotation = 0
  ScaleType = 0
  TheoreticalExact = false
  Type = 2
  UnderTolerance = 0
  X = -60
  Y = 2.5
FEATURE [TechDraw::DrawViewDimension] Dimension003
  AngleOverride = false
  Arbitrary = false
  ArbitraryTolerances = false
  EqualTolerance = true
  ExtensionAngle = 0
  FormatSpec = %.2w
  FormatSpecOverTolerance = %+.2w
  FormatSpecUnderTolerance = %+.2w
  Inverted = false
  LineAngle = 0
  LockPosition = false
  MeasureType = 1
  OverTolerance = 0
  References2D = -> [View]
  Rotation = 0
  ScaleType = 0
  TheoreticalExact = false
  Type = 1
  UnderTolerance = 0
  X = -25.5
  Y = 59.8
FEATURE [TechDraw::DrawViewDimension] Dimension004
  AngleOverride = false
  Arbitrary = false
  ArbitraryTolerances = false
  EqualTolerance = true
  ExtensionAngle = 0
  FormatSpec = %.2w
  FormatSpecOverTolerance = %+.2w
  FormatSpecUnderTolerance = %+.2w
  Inverted = false
  LineAngle = 0
  LockPosition = false
  MeasureType = 1
  OverTolerance = 0
  References2D = -> [View]
  Rotation = 0
  ScaleType = 0
  TheoreticalExact = false
  Type = 1
  UnderTolerance = 0
  X = 3.16279
  Y = 65
FEATURE [TechDraw::DrawViewPart] View004  label="Right Side View"
  CoarseView = false
  Direction = (0,-1,0)
  Focus = 100
  HardHidden = false
  IsoCount = 0
  IsoHidden = false
  IsoVisible = false
  LockPosition = false
  Perspective = false
  Rotation = 0
  ScaleType = 0
  SeamHidden = false
  SeamVisible = true
  SmoothHidden = false
  SmoothVisible = true
  Source = -> [refine]
  X = 337
  XDirection = (1,0,0)
  Y = 144.434
FEATURE [TechDraw::DrawViewSection] SectionView  label="Section  - Right Side View"
  BaseView = -> View004
  CoarseView = false
  CutSurfaceDisplay = 2
  Direction = (1,0,0)
  FileGeomPattern = C:/Program Files/FreeCAD 0.20/data/Mod/TechDraw/PAT/FCPAT.pat
  FileHatchPattern = C:/Program Files/FreeCAD 0.20/data/Mod/TechDraw/Patterns/simple.svg
  Focus = 100
  FuseBeforeCut = false
  HardHidden = false
  HatchScale = 1
  IsoCount = 0
  IsoHidden = false
  IsoVisible = false
  LockPosition = false
  NameGeomPattern = Diamond
  Perspective = false
  Rotation = 0
  ScaleType = 0
  SeamHidden = false
  SeamVisible = true
  SectionDirection = 1
  SectionNormal = (1,0,0)
  SectionOrigin = (0,0,0.57)
  SmoothHidden = false
  SmoothVisible = true
  Source = -> [refine]
  X = 337
  XDirection = (0,1,0)
  Y = 95.3651
FEATURE [TechDraw::DrawViewPart] View005  label="Left Side View"
  CoarseView = false
  Direction = (0,1,0)
  Focus = 100
  HardHidden = false
  IsoCount = 0
  IsoHidden = false
  IsoVisible = false
  LockPosition = false
  Perspective = false
  Rotation = 0
  ScaleType = 0
  SeamHidden = false
  SeamVisible = true
  SmoothHidden = false
  SmoothVisible = true
  Source = -> [refine]
  X = 198.38
  XDirection = (-1,0,0)
  Y = 145.293
FEATURE [TechDraw::DrawViewDimension] Dimension005
  AngleOverride = false
  Arbitrary = false
  ArbitraryTolerances = false
  EqualTolerance = true
  ExtensionAngle = 0
  FormatSpec = %.2w
  FormatSpecOverTolerance = %+.2w
  FormatSpecUnderTolerance = %+.2w
  Inverted = false
  LineAngle = 0
  LockPosition = false
  MeasureType = 1
  OverTolerance = 0
  References2D = -> [View005]
  Rotation = 0
  ScaleType = 0
  TheoreticalExact = false
  Type = 2
  UnderTolerance = 0
  X = -68.8132
  Y = -16.7493
FEATURE [TechDraw::DrawViewDimension] Dimension006
  AngleOverride = false
  Arbitrary = false
  ArbitraryTolerances = false
  EqualTolerance = true
  ExtensionAngle = 0
  FormatSpec = %.2w
  FormatSpecOverTolerance = %+.2w
  FormatSpecUnderTolerance = %+.2w
  Inverted = false
  LineAngle = 0
  LockPosition = false
  MeasureType = 1
  OverTolerance = 0
  References2D = -> [View005]
  Rotation = 0
  ScaleType = 0
  TheoreticalExact = false
  Type = 2
  UnderTolerance = 0
  X = -59.1984
  Y = -16.1609
FEATURE [TechDraw::DrawViewDimension] Dimension007
  AngleOverride = false
  Arbitrary = false
  ArbitraryTolerances = false
  EqualTolerance = true
  ExtensionAngle = 0
  FormatSpec = %.2w
  FormatSpecOverTolerance = %+.2w
  FormatSpecUnderTolerance = %+.2w
  Inverted = false
  LineAngle = 0
  LockPosition = false
  MeasureType = 1
  OverTolerance = 0
  References2D = -> [View005]
  Rotation = 0
  ScaleType = 0
  TheoreticalExact = false
  Type = 2
  UnderTolerance = 0
  X = 65.9673
  Y = -3.36948
FEATURE [TechDraw::DrawViewSection] SectionView001  label="Section  - Top View"
  BaseView = -> View005
  CoarseView = false
  CutSurfaceDisplay = 2
  Direction = (0,0,1)
  FileGeomPattern = C:/Program Files/FreeCAD 0.20/data/Mod/TechDraw/PAT/FCPAT.pat
  FileHatchPattern = C:/Program Files/FreeCAD 0.20/data/Mod/TechDraw/Patterns/simple.svg
  Focus = 100
  FuseBeforeCut = false
  HardHidden = false
  HatchScale = 1
  IsoCount = 0
  IsoHidden = false
  IsoVisible = false
  LockPosition = false
  NameGeomPattern = Diamond
  Perspective = false
  Rotation = 0
  ScaleType = 0
  SeamHidden = false
  SeamVisible = true
  SectionDirection = 3
  SectionNormal = (0,0,1)
  SectionOrigin = (0,0,4.75)
  SmoothHidden = false
  SmoothVisible = true
  Source = -> [refine]
  X = 198.38
  XDirection = (-1,0,0)
  Y = 69.8729
FEATURE [TechDraw::DrawViewAnnotation] Annotation
  Font = osifont
  LineSpace = 80
  LockPosition = false
  MaxWidth = -1
  Rotation = 0
  ScaleType = 0
  Text = Unit: Millimeters (mm) | - Tolerance follow ISO 2768 standards | - NO retaining sharp corners required
  TextSize = 5
  TextStyle = 0
  X = 47.6744
  Y = 118.871
FEATURE [TechDraw::DrawViewDimension] Dimension008
  AngleOverride = false
  Arbitrary = false
  ArbitraryTolerances = false
  EqualTolerance = true
  ExtensionAngle = 0
  FormatSpec = ⌀%.2w x16 (A)
  FormatSpecOverTolerance = %+.2w
  FormatSpecUnderTolerance = %+.2w
  Inverted = false
  LineAngle = 0
  LockPosition = false
  MeasureType = 1
  OverTolerance = 0
  References2D = -> [View001]
  Rotation = 0
  ScaleType = 0
  TheoreticalExact = false
  Type = 5
  UnderTolerance = 0
  X = -52.2044
  Y = 62.8757
FEATURE [TechDraw::DrawViewDimension] Dimension009
  AngleOverride = false
  Arbitrary = false
  ArbitraryTolerances = false
  EqualTolerance = true
  ExtensionAngle = 0
  FormatSpec = ⌀%.2w x16 (A)
  FormatSpecOverTolerance = %+.2w
  FormatSpecUnderTolerance = %+.2w
  Inverted = false
  LineAngle = 0
  LockPosition = false
  MeasureType = 1
  OverTolerance = 0
  References2D = -> [View004]
  Rotation = 0
  ScaleType = 0
  TheoreticalExact = false
  Type = 5
  UnderTolerance = 0
  X = 64.7317
  Y = 24.9242
FEATURE [TechDraw::DrawViewDimension] Dimension011
  AngleOverride = false
  Arbitrary = false
  ArbitraryTolerances = false
  EqualTolerance = true
  ExtensionAngle = 0
  FormatSpec = ⌀%.2w
  FormatSpecOverTolerance = %+.2w
  FormatSpecUnderTolerance = %+.2w
  Inverted = false
  LineAngle = 0
  LockPosition = false
  MeasureType = 1
  OverTolerance = 0
  References2D = -> [View001]
  Rotation = 0
  ScaleType = 0
  TheoreticalExact = false
  Type = 5
  UnderTolerance = 0
  X = -63.2548
  Y = -4.15759
FEATURE [TechDraw::DrawViewDimension] Dimension012
  AngleOverride = false
  Arbitrary = false
  ArbitraryTolerances = false
  EqualTolerance = true
  ExtensionAngle = 0
  FormatSpec = %.2w
  FormatSpecOverTolerance = %+.2w
  FormatSpecUnderTolerance = %+.2w
  Inverted = false
  LineAngle = 0
  LockPosition = false
  MeasureType = 1
  OverTolerance = 0
  References2D = -> [SectionView]
  Rotation = 0
  ScaleType = 0
  TheoreticalExact = false
  Type = 6
  UnderTolerance = 0
  X = 23.8692
  Y = 20.7861
FEATURE [TechDraw::DrawViewDimension] Dimension013
  AngleOverride = false
  Arbitrary = false
  ArbitraryTolerances = false
  EqualTolerance = true
  ExtensionAngle = 0
  FormatSpec = %.2w
  FormatSpecOverTolerance = %+.2w
  FormatSpecUnderTolerance = %+.2w
  Inverted = false
  LineAngle = 0
  LockPosition = false
  MeasureType = 1
  OverTolerance = 0
  References2D = -> [SectionView]
  Rotation = 0
  ScaleType = 0
  TheoreticalExact = false
  Type = 2
  UnderTolerance = 0
  X = 67.9639
  Y = -3.89171
FEATURE [TechDraw::DrawViewDimension] Dimension014
  AngleOverride = false
  Arbitrary = false
  ArbitraryTolerances = false
  EqualTolerance = true
  ExtensionAngle = 0
  FormatSpec = %.2w
  FormatSpecOverTolerance = %+.2w
  FormatSpecUnderTolerance = %+.2w
  Inverted = false
  LineAngle = 0
  LockPosition = false
  MeasureType = 1
  OverTolerance = 0
  References2D = -> [SectionView]
  Rotation = 0
  ScaleType = 0
  TheoreticalExact = false
  Type = 2
  UnderTolerance = 0
  X = 59.7966
  Y = 16.1909
FEATURE [TechDraw::DrawViewDimension] Dimension015
  AngleOverride = false
  Arbitrary = false
  ArbitraryTolerances = false
  EqualTolerance = true
  ExtensionAngle = 0
  FormatSpec = ⌀%.2w
  FormatSpecOverTolerance = %+.2w
  FormatSpecUnderTolerance = %+.2w
  Inverted = false
  LineAngle = 0
  LockPosition = false
  MeasureType = 1
  OverTolerance = 0
  References2D = -> [View]
  Rotation = 0
  ScaleType = 0
  TheoreticalExact = false
  Type = 5
  UnderTolerance = 0
  X = -30.7448
  Y = -26.0111
FEATURE [TechDraw::DrawViewDimension] Dimension016
  AngleOverride = false
  Arbitrary = false
  ArbitraryTolerances = false
  EqualTolerance = true
  ExtensionAngle = 0
  FormatSpec = ⌀%.2w x3 (B)
  FormatSpecOverTolerance = %+.2w
  FormatSpecUnderTolerance = %+.2w
  Inverted = false
  LineAngle = 0
  LockPosition = false
  MeasureType = 1
  OverTolerance = 0
  References2D = -> [View]
  Rotation = 0
  ScaleType = 0
  TheoreticalExact = false
  Type = 5
  UnderTolerance = 0
  X = 0.687433
  Y = -14.9517
FEATURE [TechDraw::DrawViewDimension] Dimension017
  AngleOverride = false
  Arbitrary = false
  ArbitraryTolerances = false
  EqualTolerance = true
  ExtensionAngle = 0
  FormatSpec = %.2w
  FormatSpecOverTolerance = %+.2w
  FormatSpecUnderTolerance = %+.2w
  Inverted = false
  LineAngle = 0
  LockPosition = false
  MeasureType = 1
  OverTolerance = 0
  References2D = -> [View]
  Rotation = 0
  ScaleType = 0
  TheoreticalExact = false
  Type = 1
  UnderTolerance = 0
  X = 24.2111
  Y = 59.804
FEATURE [TechDraw::DrawViewAnnotation] Annotation001
  Font = osifont
  LineSpace = 80
  LockPosition = false
  MaxWidth = -1
  Rotation = 0
  ScaleType = 0
  Text = Type (A) holes are threaded for M2.5 screws | - Total number of type (A) hole: 32 | |---- Vertical: 16 | |---- Side: 16
  TextSize = 5
  TextStyle = 0
  X = 54.7229
  Y = 73.7648
FEATURE [TechDraw::DrawViewAnnotation] Annotation002
  Font = osifont
  LineSpace = 80
  LockPosition = false
  MaxWidth = -1
  Rotation = 0
  ScaleType = 0
  Text = Type (B) holes are threaded for Torx Flathead M6 screws | - Total number of type (B) hole: 3 | |---- Vertical: 3 | |---- Side: 0
  TextSize = 5
  TextStyle = 0
  X = 68.2777
  Y = 30.031
FEATURE [TechDraw::DrawViewAnnotation] Annotation003
  Font = Ubuntu
  LineSpace = 80
  LockPosition = false
  MaxWidth = -1
  Rotation = 0
  ScaleType = 0
  Text = OpenSCAD_MyChassisModeling_NewBottom_version-cnes.stl | Modified: Jan 08, 2024 | By: mtnguyen
  TextSize = 5
  TextStyle = 2
  X = 348.584
  Y = 7.96372
FEATURE [TechDraw::DrawViewDimension] Dimension018
  AngleOverride = false
  Arbitrary = false
  ArbitraryTolerances = false
  EqualTolerance = true
  ExtensionAngle = 0
  FormatSpec = %.2w
  FormatSpecOverTolerance = %+.2w
  FormatSpecUnderTolerance = %+.2w
  Inverted = false
  LineAngle = 0
  LockPosition = false
  MeasureType = 1
  OverTolerance = 0
  References2D = -> [SectionView]
  Rotation = 0
  ScaleType = 0
  TheoreticalExact = false
  Type = 1
  UnderTolerance = 0
  X = 35.9647
  Y = -7.04264
FEATURE [TechDraw::DrawViewDimension] Dimension019
  AngleOverride = false
  Arbitrary = false
  ArbitraryTolerances = false
  EqualTolerance = true
  ExtensionAngle = 0
  FormatSpec = %.2w
  FormatSpecOverTolerance = %+.2w
  FormatSpecUnderTolerance = %+.2w
  Inverted = false
  LineAngle = 0
  LockPosition = false
  MeasureType = 1
  OverTolerance = 0
  References2D = -> [SectionView]
  Rotation = 0
  ScaleType = 0
  TheoreticalExact = false
  Type = 1
  UnderTolerance = 0
  X = 37.49
  Y = -13.6669
FEATURE [TechDraw::DrawPage] Page
  KeepUpdated = true
  NextBalloonIndex = 1
  ProjectionType = 0
  Template = -> Template
  Views = -> [View,View001,View003,Dimension,Dimension001,Dimension003,Dimension004,View004,SectionView,View005,Dimension005,Dimension006,Dimension007,SectionView001,Annotation,Dimension008,Dimension009,Dimension011,Dimension012,Dimension013,Dimension014,Dimension015,Dimension016,Dimension017,Annotation001,Annotation002,Annotation003,Dimension018,Dimension019]
